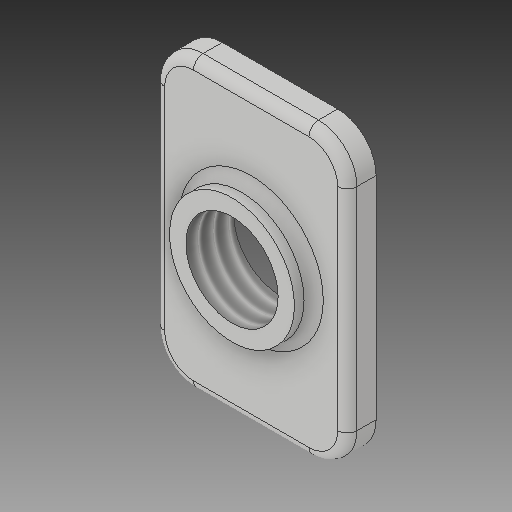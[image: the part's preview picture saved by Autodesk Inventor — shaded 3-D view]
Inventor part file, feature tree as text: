
AUTODESK INVENTOR PART (.ipt)
format: ipt  version: 2018 (Build 220112000, 112)  size: 178,176 bytes
history: native  units: mm
features: other x3, sketch x2
ambient origin geometry x8: Origin, YZ Plane, XZ Plane, XY Plane, X Axis, Y Axis, Z Axis, Center Point
bodies: Solid1 (feature_tree)
feature tree (5):
  other  "M5 Tee Nut-Generic_MIR_CPY.ipt"
  other  "Solid1::M5 Tee Nut-Generic_MIR_CPY.ipt"
  other  "TaggingFeature1"
  sketch  "Sketch1"  dims[d0=10.0mm]
  sketch  "Sketch2"
